# Revit family: NLRS_33_GM_FB_TC_STORAX_vloerluik_VLB_BCB
name_source: partatom
category: Generic Models
revit_build: Autodesk Revit 2014 (Build: 20130308_1515(x64)
units: mm (PartAtom-declared; Revit-internal decimal feet)

## types (4) — shared parameters
Manufacturer = Storax
Model = BV
URL = http://www.storax.nl
belasting = 300 kg
brandwerend 90 min = nee
gasdrukveer = nee
geïsoleerd = ja
materiaal = bcb_rvs
productgroep = Vloerluiken
rubberen_afdichting = enkel
scharnierend = nee
sluiting = 0
vergrendeling = nee
zero-valued in all types: Default Elevation

## per-type parameters (varying)
| type | binnenmaat_breedte | binnenmaat_lengte | gewicht | uitwendige_breedte | uitwendige_lengte |
| maatwerk | 395 mm | 595 mm | 10 | 449 mm | 649 mm  [stored 2.12927 ft] |
| VLB 64 | 395 mm | 595 mm |  | 449 mm | 649 mm  [stored 2.12927 ft] |
| VLB 75 | 495 mm | 695 mm |  | 549 mm | 749 mm  [stored 2.45735 ft] |
| VLB 86 | 595 mm | 695 mm |  | 649 mm  [stored 2.12927 ft] | 749 mm  [stored 2.45735 ft] |

note: [stored X ft] marks values corroborated as IEEE doubles in the binary element streams (Revit-internal decimal feet)

## geometry (parser evidence)
native form markers: Blend x766, Sweep x7
no freeform markers — native parametric forms only
